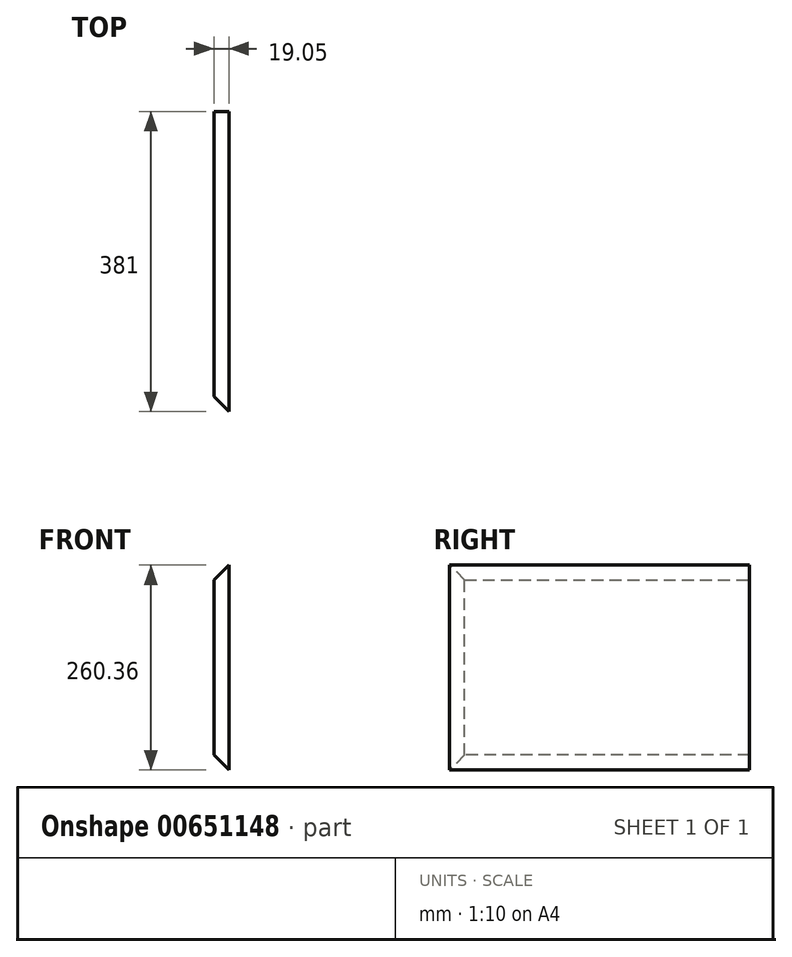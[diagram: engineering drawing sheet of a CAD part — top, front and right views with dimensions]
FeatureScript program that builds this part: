
annotation { "Feature Type Name" : "Feature", "Feature Type Description" : "" }
export const myFeature = defineFeature(function(context is Context, id is Id, definition is map)
    precondition{}
    {
        {
            var Q0;
            Q0=qCreatedBy(makeId("Right.planeOp"),FACE);
            var sketch = newSketch(context, id + "F0", { "sketchPlane" : qUnion([Q0])});
            skLineSegment(sketch, "E0.bottom", {"start": v(190.5, 130.18) * mm, "end": v(-190.5, 130.18) * mm});
            skLineSegment(sketch, "E0.top", {"start": v(190.5, -130.18) * mm, "end": v(-190.5, -130.18) * mm});
            skLineSegment(sketch, "E0.left", {"start": v(190.5, 130.18) * mm, "end": v(190.5, -130.18) * mm});
            skLineSegment(sketch, "E0.right", {"start": v(-190.5, 130.18) * mm, "end": v(-190.5, -130.18) * mm});
            skPoint(sketch, "E0.middle", {"position": v(0, 0) * mm});
            skSolve(sketch);
        }
        {
            var Q0;
            Q0=makeQuery(id+"F0.imprint","IMPRINT",FACE,{"disambiguationData":[TD([[makeQuery(id+"F0.imprint","IMPRINT",EDGE,{"derivedFrom":sQuery(id+"F0.wireOp",EDGE,"E0.bottom")}),1.0]])]});
            extrude(context, id + "F1", {"entities" : qUnion([Q0]), "depth" : 19.05 * mm, "offsetDistance" : 25.4 * mm});
        }
        {
            var Q0;
            Q0=makeQuery(id+"F1.opExtrude","CAP_EDGE",EDGE,{"disambiguationData":[OSD([sQuery(id+"F0.wireOp",EDGE,"E0.top")])],"isStart":true});
            var Q1;
            Q1=makeQuery(id+"F1.opExtrude","CAP_EDGE",EDGE,{"disambiguationData":[OSD([sQuery(id+"F0.wireOp",EDGE,"E0.bottom")])],"isStart":true});
            var Q2;
            Q2=makeQuery(id+"F1.opExtrude","CAP_EDGE",EDGE,{"disambiguationData":[OSD([sQuery(id+"F0.wireOp",EDGE,"E0.right")])],"isStart":true});
            chamfer(context, id + "F2", {"entities" : qUnion([Q0, Q1, Q2]), "width" : 19.05 * mm, "tangentPropagation" : true});
        }
    });
